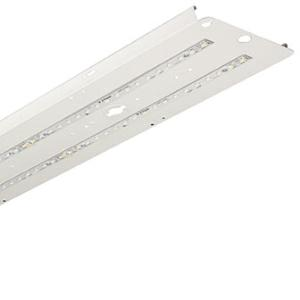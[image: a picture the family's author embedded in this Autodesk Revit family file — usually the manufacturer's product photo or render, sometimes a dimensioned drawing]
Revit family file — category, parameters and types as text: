
# Revit family: 3f_filippi_-_kit_led_retrofit_per_schermo_in_vetro_3f_filippi_-_a5117_-_kit_led_i3f_76__a3f_91_-_l1565-2x30w_ca88
name_source: partatom
category: Lighting Fixtures
units: mm (PartAtom-declared; Revit-internal decimal feet)

## family parameters
Cut with Voids When Loaded = No
Host = Face
Light Source = No
Part Type = Normal
Room Calculation Point = No
Round Connector Dimension = Use Diameter
Shared = No

## types (1)
- 3F Filippi - Kit LED Retrofit per schermo in vetro (1 x LED, 9058 lm, 66 W, 4000 K)
    Apparent Load = 66 VA
    Approval mark = ENEC
    CIE Flux Codes = 52 87 99 100 100
    Color Rendering = 80
    Color Temperature = 4000 K
    Control Gear = Electronic ballast
    Default Elevation = 1800 mm
    Description = Led retrofit kit suitable for Fluorescent Beta 2x i3F 76 and A3F 91 luminaires.

ILLUMINOTECHNICAL
Luminous efficiency 100% (DLOR 100%, ULOR 0%).
Initial luminous flux of the luminaire 9058 lm.
Symmetric distribution.
Installation Interdistance Transv.D = 1.29 x hu - Long.D = 1.29 x hu.
Tabular UGR (CIE 117 - 4H-8H; S=0.25H; 70/50/20): RUG 21.1 - 23.8.
Beam angle: 106° - 113°.
Luminous efficacy 137 lm/W.
Lifetime (L93/B10): 30000 h. (tq+25°C)
Lifetime (L90/B10): 50000 h. (tq+25°C)
Lifetime (L85/B10): 80000 h. (tq+25°C)
Lifetime (L80/B10): 100000 h. (tq+25°C)
Lifetime (L85/B10): 50000 h. (tq+35°C)
Sudden decreased luminous flux after 50000 hours: 0% (C0).
Photobiological safety in compliance with IEC/TR 62778: RG0 risk exempt, (IEC 62471).
In compliance with IEC/EN 62722-2-1 - IEC/EN 62717 standards.

SOURCE
2 linear LED modules 30W/840.
Energy efficiency class (UE 2019/2020 - UE 2019/2015): D.
CIE 13.3 Colour rendering index: CRI >80 (R9 <50%).
IES TM-30 Fidelity Index: Rf = 84 Rg = 95.
CCT nominal colour temperature 4000 K.
Colour initial tolerance (MacAdam): SDCM 3.

MECHANICAL
Gear-tray unit in hot-galvanised steel, painted in white polyester, fixed to the housing by means of "Ribloc" rapid devices in galvanised steel, hinged opening.
Luminaire with limited surface temperature. - D - (EN 60598-2-24)
Dimensions: 1565x235 mm, height 105 mm. Weight 1.92 kg.
Glow-wire test resistance 850°C.

ELECTRICAL
Halogen Free electronic wiring 230V-50/60Hz, power factor 0.97, THD <25%, constant output current, SELV, class I, 1 driver.
Power of the luminaire 66 W.
CE - IEC 60598-1 - EN 60598-1.
SAFE FLICKER: PstLM=<1 and SVM=<0.4 (IEC TR 61547-1 and IEC TR 63158), to ensure a more comfortable and safe light.
Luminaire compliant with EN 60598-2-22 for power supply from a centralised emergency system CPSS (Central Power Supply System), not incorporated in the luminaire - high risk areas excluded. The default power and flux are 100% in AC and 100% in DC.
Ambient temperature from -20°C to +35°C.
Temperature class T6 max 85°C.
Relative humidity UR: <85%.

INSTALLATION
Retrofit.
Correct installation of the retrofit LED kit, compliant with EN 60598-1 and CE marked, inside the 3F Filippi - Beta 2x i3F 76, A3F 91 and A3F 93 Fluorescent luminaires must be only carried out by qualified personnel to ensure compliance with the national installation standards.
Attention: to maintain the degree of protection of the device and for the purposes of validity of the guarantee of the new retrofit kits, it is imperative to replace the old cable guides (on the body of the device) with the new ones supplied.
All accessories dedicated to this product are available on the Catalog and on our website www.3F-Filippi.com.

WARNING
Fixture not suitable for cold stores with an ambient temperature <0°C and/or relative humidity >85%.
Luminaire designed for disposal/recycling at end-of-life.
Replaceable (LED only) light source by a professional. Replaceable control gear by a professional.
    Height = 105 mm
    Lamp = 1 x LED
    Lamp Light Flux = 9058 lm
    Lamp Power = 66 W
    Lamp count = 1
    Length = 1565 mm
    Lifetime = 50000 h
    Luminous efficacy = 137 lm/W
    Manufacturer = 3F Filippi
    ModVariant = No
    Model = 3F Filippi - A5117 - KIT LED i3F 76, A3F 91 - L1565-2x30W
    Mounting Place = Ceiling
    Mounting Type = Surface mounted
    Number of Poles = 1
    OnlyDefault = Yes
    Power Factor = 1
    Product Name = 3F Filippi - Kit LED Retrofit per schermo in vetro
    Product group = ceiling mounted luminaire
    ProductGroupID = 3
    Protection Class = Protection class I
    Protection Degree = Degree of protection
    RLX_Detail_Level = 1
    RLX_Emergency_Light_Flux = 0 lm
    RLX_Emergency_Type = 0
    RLX_Emergency_Type_DB = No
    RlxData = <blob elided: 57985 chars, md5=bb279879>
    Socket = socket
    Standby Power = 0 W
    System Light Flux = 9058 lm
    System Power = 66 W
    Type Comments = Product without accessories
    Type Image = 3ffilippi_a5117.jpg
    URL = http://relux.com
    VarID = ---
    Voltage = 0 V
    Weight = 0.00 kg
    Width = 235 mm

## geometry (parser evidence)
native form markers: Blend x4, Sweep x9
no freeform markers — native parametric forms only
